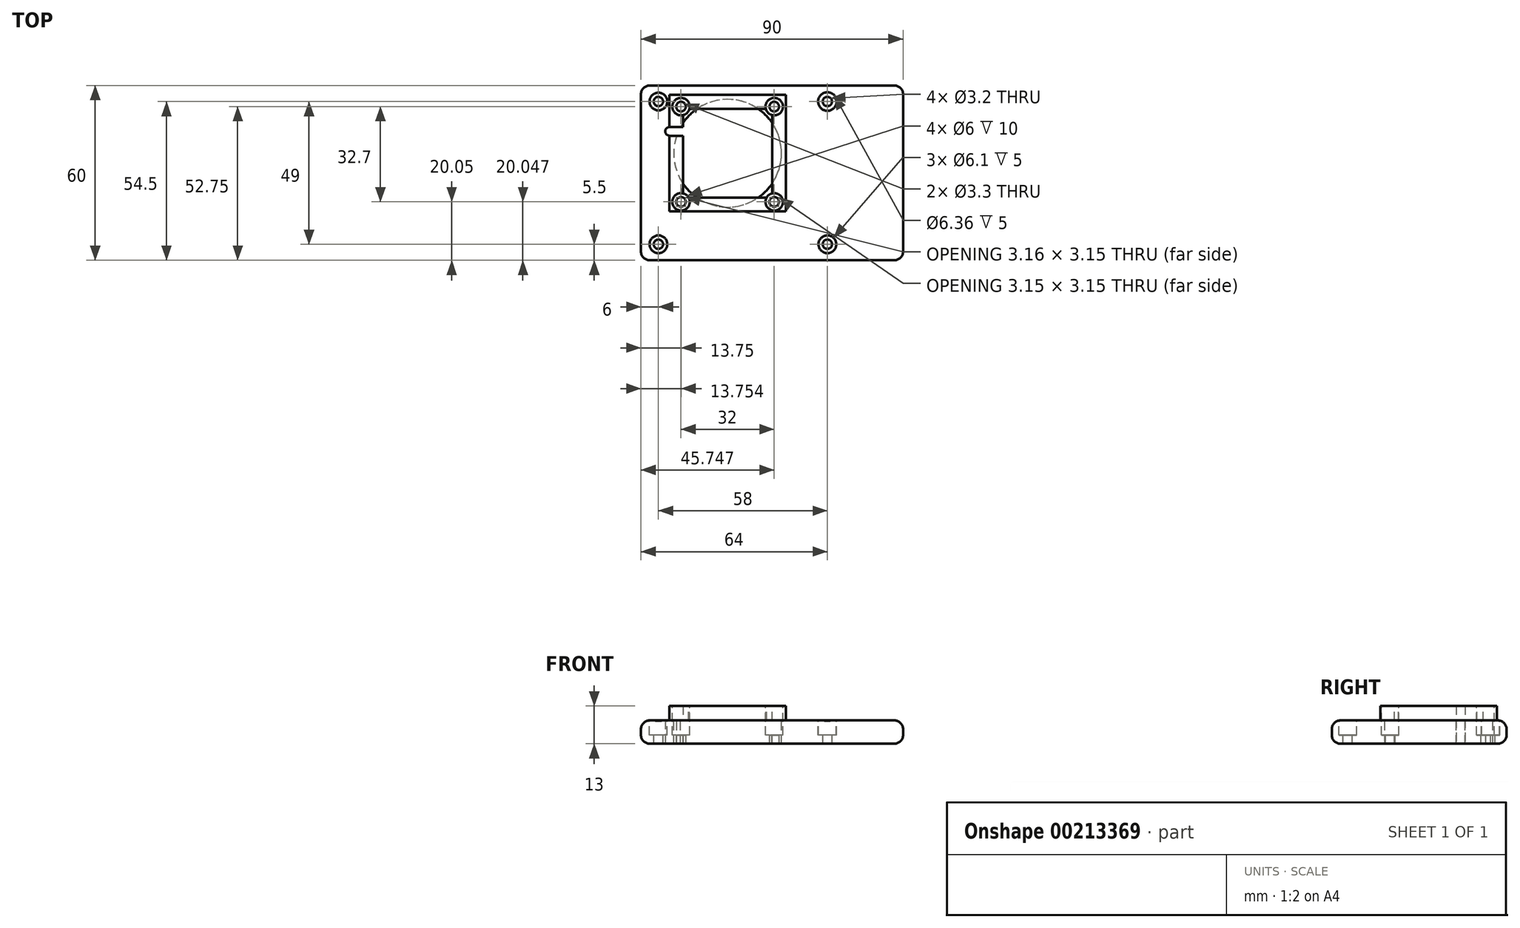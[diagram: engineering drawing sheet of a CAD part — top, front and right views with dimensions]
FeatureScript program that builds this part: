
annotation { "Feature Type Name" : "Feature", "Feature Type Description" : "" }
export const myFeature = defineFeature(function(context is Context, id is Id, definition is map)
    precondition{}
    {
        {
            var Q0;
            Q0=qCreatedBy(makeId("Top.planeOp"),FACE);
            var sketch = newSketch(context, id + "F0", { "sketchPlane" : qUnion([Q0])});
            skLineSegment(sketch, "E0.bottom", {"start": v(-45.78, -23.25) * mm, "end": v(38.22, -23.25) * mm});
            skLineSegment(sketch, "E0.top", {"start": v(-45.78, 36.75) * mm, "end": v(38.22, 36.75) * mm});
            skLineSegment(sketch, "E0.left", {"start": v(-48.78, -20.25) * mm, "end": v(-48.78, 33.75) * mm});
            skLineSegment(sketch, "E0.right", {"start": v(41.22, -20.25) * mm, "end": v(41.22, 33.75) * mm});
            skPoint(sketch, "E1.visualSharp", {"position": v(-48.78, 36.75) * mm});
            skArc(sketch, "E1.filletArc", {"start": v(-45.78, 36.75) * mm, "mid": v(-47.9, 35.87) * mm, "end": v(-48.78, 33.75) * mm});
            skPoint(sketch, "E2.visualSharp", {"position": v(41.22, 36.75) * mm});
            skArc(sketch, "E2.filletArc", {"start": v(41.22, 33.75) * mm, "mid": v(40.34, 35.87) * mm, "end": v(38.22, 36.75) * mm});
            skPoint(sketch, "E3.visualSharp", {"position": v(41.22, -23.25) * mm});
            skArc(sketch, "E3.filletArc", {"start": v(38.22, -23.25) * mm, "mid": v(40.34, -22.37) * mm, "end": v(41.22, -20.25) * mm});
            skPoint(sketch, "E4.visualSharp", {"position": v(-48.78, -23.25) * mm});
            skArc(sketch, "E4.filletArc", {"start": v(-48.78, -20.25) * mm, "mid": v(-47.9, -22.37) * mm, "end": v(-45.78, -23.25) * mm});
            skCircle(sketch, "E5", {"center": v(-42.78, -17.75) * mm, "radius": 1.6 * mm});
            skCircle(sketch, "E6", {"center": v(15.22, -17.75) * mm, "radius": 1.6 * mm});
            skCircle(sketch, "E7", {"center": v(-42.78, 31.25) * mm, "radius": 1.6 * mm});
            skCircle(sketch, "E8", {"center": v(15.22, 31.25) * mm, "radius": 1.6 * mm});
            skPoint(sketch, "E9", {"position": v(-29.78, 8.98) * mm});
            skPoint(sketch, "E10", {"position": v(2.22, -23.02) * mm});
            skLineSegment(sketch, "E11.bottom", {"start": v(-44.03, -20.25) * mm, "end": v(5.97, -20.25) * mm});
            skLineSegment(sketch, "E11.top", {"start": v(-44.03, 24.75) * mm, "end": v(5.97, 24.75) * mm});
            skLineSegment(sketch, "E11.left", {"start": v(-44.03, -20.25) * mm, "end": v(-44.03, 24.75) * mm});
            skLineSegment(sketch, "E11.right", {"start": v(5.97, -20.25) * mm, "end": v(5.97, 24.75) * mm});
            skLineSegment(sketch, "E12.bottom", {"start": v(-34.28, -15.25) * mm, "end": v(-3.78, -15.25) * mm});
            skLineSegment(sketch, "E12.top", {"start": v(-34.28, 15.25) * mm, "end": v(-3.78, 15.25) * mm});
            skLineSegment(sketch, "E12.left", {"start": v(-34.28, -15.25) * mm, "end": v(-34.28, 15.25) * mm});
            skLineSegment(sketch, "E12.right", {"start": v(-3.78, -15.25) * mm, "end": v(-3.78, 15.25) * mm});
            skCircle(sketch, "E13", {"center": v(-19.03, 0) * mm, "radius": 18.5 * mm});
            skLineSegment(sketch, "E14.bottom", {"start": v(0.97, 20) * mm, "end": v(-39.03, 20) * mm});
            skLineSegment(sketch, "E14.top", {"start": v(0.97, -20) * mm, "end": v(-39.03, -20) * mm});
            skLineSegment(sketch, "E14.left", {"start": v(0.97, 20) * mm, "end": v(0.97, -20) * mm});
            skLineSegment(sketch, "E14.right", {"start": v(-39.03, 20) * mm, "end": v(-39.03, -20) * mm});
            skCircle(sketch, "E15", {"center": v(-35.03, -16) * mm, "radius": 1.65 * mm});
            skCircle(sketch, "E16", {"center": v(-35.03, 16.7) * mm, "radius": 1.65 * mm});
            skCircle(sketch, "E17", {"center": v(-3.03, -16) * mm, "radius": 1.65 * mm});
            skCircle(sketch, "E18", {"center": v(-3.03, 16.7) * mm, "radius": 1.65 * mm});
            skCircle(sketch, "E19", {"center": v(15.22, 31.25) * mm, "radius": 3.05 * mm});
            skCircle(sketch, "E20", {"center": v(15.22, -17.75) * mm, "radius": 3.18 * mm});
            skCircle(sketch, "E21", {"center": v(-42.78, -17.75) * mm, "radius": 3.05 * mm});
            skCircle(sketch, "E22", {"center": v(-42.78, 31.25) * mm, "radius": 3.05 * mm});
            skLineSegment(sketch, "E23", {"start": v(-57.92, 59.7) * mm, "end": v(47.25, 59.7) * mm});
            skSolve(sketch);
        }
        {
            var Q0;
            {var subQ0=sQuery(id+"F0.wireOp",EDGE,"E13");var subQ1=sQuery(id+"F0.wireOp",EDGE,"E12.bottom");var subQ2=makeQuery(id+"F0.imprint","INTERSECT",VERTEX,{"disambiguationData":[OD(0.0)],"derivedFrom":[subQ1,subQ0]});Q0=makeQuery(id+"F0.imprint","IMPRINT",FACE,{"disambiguationData":[TD([[makeQuery(id+"F0.imprint","IMPRINT",EDGE,{"disambiguationData":[TD([[subQ2,-1.0]])],"derivedFrom":subQ1}),-1.0]])]});}
            var Q1;
            {var subQ0=sQuery(id+"F0.wireOp",EDGE,"E13");var subQ1=sQuery(id+"F0.wireOp",EDGE,"E12.right");var subQ2=makeQuery(id+"F0.imprint","INTERSECT",VERTEX,{"disambiguationData":[OD(0.0)],"derivedFrom":[subQ1,subQ0]});Q1=makeQuery(id+"F0.imprint","IMPRINT",FACE,{"disambiguationData":[TD([[makeQuery(id+"F0.imprint","IMPRINT",EDGE,{"disambiguationData":[TD([[subQ2,-1.0]])],"derivedFrom":subQ1}),-1.0]])]});}
            var Q2;
            {var subQ0=sQuery(id+"F0.wireOp",EDGE,"E13");var subQ1=sQuery(id+"F0.wireOp",EDGE,"E12.top");var subQ2=makeQuery(id+"F0.imprint","INTERSECT",VERTEX,{"disambiguationData":[OD(0.0)],"derivedFrom":[subQ1,subQ0]});Q2=makeQuery(id+"F0.imprint","IMPRINT",FACE,{"disambiguationData":[TD([[makeQuery(id+"F0.imprint","IMPRINT",EDGE,{"disambiguationData":[TD([[subQ2,-1.0]])],"derivedFrom":subQ1}),1.0]])]});}
            var Q3;
            {var subQ0=sQuery(id+"F0.wireOp",EDGE,"E13");var subQ1=sQuery(id+"F0.wireOp",EDGE,"E12.left");var subQ2=makeQuery(id+"F0.imprint","INTERSECT",VERTEX,{"disambiguationData":[OD(0.0)],"derivedFrom":[subQ1,subQ0]});Q3=makeQuery(id+"F0.imprint","IMPRINT",FACE,{"disambiguationData":[TD([[makeQuery(id+"F0.imprint","IMPRINT",EDGE,{"disambiguationData":[TD([[subQ2,-1.0]])],"derivedFrom":subQ1}),1.0]])]});}
            var Q4;
            Q4=makeQuery(id+"F0.imprint","IMPRINT",FACE,{"disambiguationData":[TD([[makeQuery(id+"F0.imprint","IMPRINT",EDGE,{"derivedFrom":sQuery(id+"F0.wireOp",EDGE,"E14.bottom")}),1.0]])]});
            extrude(context, id + "F1", {"entities" : qUnion([Q0, Q1, Q2, Q3, Q4]), "depth" : 5 * mm});
        }
        {
            var Q0;
            Q0=makeQuery(id+"F0.imprint","IMPRINT",FACE,{"disambiguationData":[TD([[makeQuery(id+"F0.imprint","IMPRINT",EDGE,{"derivedFrom":sQuery(id+"F0.wireOp",EDGE,"E0.bottom")}),1.0]])]});
            var Q1;
            {var subQ6=sQuery(id+"F0.wireOp",EDGE,"E11.bottom");Q1=makeQuery(id+"F0.imprint","IMPRINT",FACE,{"disambiguationData":[TD([[makeQuery(id+"F0.imprint","IMPRINT",EDGE,{"derivedFrom":subQ6}),1.0]])]});}
            var Q2;
            {var subQ0=sQuery(id+"F0.wireOp",EDGE,"E12.right");var subQ1=sQuery(id+"F0.wireOp",EDGE,"E12.top");var subQ2=makeQuery(id+"F0.imprint","INTERSECT",VERTEX,{"derivedFrom":[subQ1,subQ0]});Q2=makeQuery(id+"F0.imprint","IMPRINT",FACE,{"disambiguationData":[TD([[makeQuery(id+"F0.imprint","IMPRINT",EDGE,{"disambiguationData":[TD([[subQ2,1.0]])],"derivedFrom":subQ1}),-1.0]])]});}
            var Q3;
            {var subQ0=sQuery(id+"F0.wireOp",EDGE,"E12.left");var subQ1=sQuery(id+"F0.wireOp",EDGE,"E12.top");var subQ2=makeQuery(id+"F0.imprint","INTERSECT",VERTEX,{"derivedFrom":[subQ1,subQ0]});Q3=makeQuery(id+"F0.imprint","IMPRINT",FACE,{"disambiguationData":[TD([[makeQuery(id+"F0.imprint","IMPRINT",EDGE,{"disambiguationData":[TD([[subQ2,-1.0]])],"derivedFrom":subQ1}),-1.0]])]});}
            var Q4;
            {var subQ0=sQuery(id+"F0.wireOp",EDGE,"E13");var subQ1=sQuery(id+"F0.wireOp",EDGE,"E12.bottom");var subQ2=makeQuery(id+"F0.imprint","INTERSECT",VERTEX,{"disambiguationData":[OD(1.0)],"derivedFrom":[subQ1,subQ0]});Q4=makeQuery(id+"F0.imprint","IMPRINT",FACE,{"disambiguationData":[TD([[makeQuery(id+"F0.imprint","IMPRINT",EDGE,{"disambiguationData":[TD([[subQ2,-1.0]])],"derivedFrom":subQ1}),1.0]])]});}
            var Q5;
            {var subQ0=sQuery(id+"F0.wireOp",EDGE,"E13");var subQ1=sQuery(id+"F0.wireOp",EDGE,"E12.top");var subQ2=makeQuery(id+"F0.imprint","INTERSECT",VERTEX,{"disambiguationData":[OD(1.0)],"derivedFrom":[subQ1,subQ0]});Q5=makeQuery(id+"F0.imprint","IMPRINT",FACE,{"disambiguationData":[TD([[makeQuery(id+"F0.imprint","IMPRINT",EDGE,{"disambiguationData":[TD([[subQ2,-1.0]])],"derivedFrom":subQ1}),-1.0]])]});}
            var Q6;
            {var subQ0=sQuery(id+"F0.wireOp",EDGE,"E16");var subQ1=sQuery(id+"F0.wireOp",EDGE,"E12.top");var subQ2=makeQuery(id+"F0.imprint","INTERSECT",VERTEX,{"derivedFrom":[subQ1,subQ0]});Q6=makeQuery(id+"F0.imprint","IMPRINT",FACE,{"disambiguationData":[TD([[makeQuery(id+"F0.imprint","IMPRINT",EDGE,{"disambiguationData":[TD([[subQ2,-1.0]])],"derivedFrom":subQ1}),-1.0]])]});}
            var Q7;
            {var subQ0=sQuery(id+"F0.wireOp",EDGE,"E15");var subQ1=sQuery(id+"F0.wireOp",EDGE,"E12.bottom");var subQ2=makeQuery(id+"F0.imprint","INTERSECT",VERTEX,{"derivedFrom":[subQ1,subQ0]});Q7=makeQuery(id+"F0.imprint","IMPRINT",FACE,{"disambiguationData":[TD([[makeQuery(id+"F0.imprint","IMPRINT",EDGE,{"disambiguationData":[TD([[subQ2,-1.0]])],"derivedFrom":subQ1}),1.0]])]});}
            var Q8;
            Q8=makeQuery(id+"F0.imprint","IMPRINT",FACE,{"disambiguationData":[TD([[makeQuery(id+"F0.imprint","IMPRINT",EDGE,{"derivedFrom":sQuery(id+"F0.wireOp",EDGE,"E14.bottom")}),1.0]])]});
            var Q9;
            Q9=makeQuery(id+"F0.imprint","IMPRINT",FACE,{"disambiguationData":[TD([[makeQuery(id+"F0.imprint","IMPRINT",EDGE,{"derivedFrom":sQuery(id+"F0.wireOp",EDGE,"E5")}),-1.0]])]});
            var Q10;
            Q10=makeQuery(id+"F0.imprint","IMPRINT",FACE,{"disambiguationData":[TD([[makeQuery(id+"F0.imprint","IMPRINT",EDGE,{"derivedFrom":sQuery(id+"F0.wireOp",EDGE,"E6")}),-1.0]])]});
            var Q11;
            Q11=makeQuery(id+"F0.imprint","IMPRINT",FACE,{"disambiguationData":[TD([[makeQuery(id+"F0.imprint","IMPRINT",EDGE,{"derivedFrom":sQuery(id+"F0.wireOp",EDGE,"E8")}),-1.0]])]});
            var Q12;
            {var subQ2=sQuery(id+"F0.wireOp",EDGE,"E11.top");Q12=makeQuery(id+"F0.imprint","IMPRINT",FACE,{"disambiguationData":[TD([[makeQuery(id+"F0.imprint","IMPRINT",EDGE,{"derivedFrom":subQ2}),-1.0]])]});}
            var Q13;
            Q13=makeQuery(id+"F0.imprint","IMPRINT",FACE,{"disambiguationData":[TD([[makeQuery(id+"F0.imprint","IMPRINT",EDGE,{"derivedFrom":sQuery(id+"F0.wireOp",EDGE,"E7")}),-1.0]])]});
            extrude(context, id + "F2", {"entities" : qUnion([Q0, Q1, Q2, Q3, Q4, Q5, Q6, Q7, Q8, Q9, Q10, Q11, Q12, Q13]), "operationType" : NewBodyOperationType.ADD, "oppositeDirection" : true, "depth" : 8 * mm});
        }
        {
            var Q0;
            Q0=makeQuery(id+"F1.opExtrude","CAP_FACE",FACE,{"disambiguationData":[OSD([sQuery(id+"F0.wireOp",EDGE,"E7"),sQuery(id+"F0.wireOp",EDGE,"E11.bottom"),sQuery(id+"F0.wireOp",EDGE,"E11.top"),sQuery(id+"F0.wireOp",EDGE,"E11.left"),sQuery(id+"F0.wireOp",EDGE,"E11.right"),sQuery(id+"F0.wireOp",EDGE,"E12.bottom"),sQuery(id+"F0.wireOp",EDGE,"E12.top"),sQuery(id+"F0.wireOp",EDGE,"E12.left"),sQuery(id+"F0.wireOp",EDGE,"E12.right"),sQuery(id+"F0.wireOp",EDGE,"E15"),sQuery(id+"F0.wireOp",EDGE,"E16"),sQuery(id+"F0.wireOp",EDGE,"E17"),sQuery(id+"F0.wireOp",EDGE,"E18")])],"isStart":false});
            var sketch = newSketch(context, id + "F3", { "sketchPlane" : qUnion([Q0])});
            skCircle(sketch, "E24", {"center": v(-35.03, 16.7) * mm, "radius": 3 * mm});
            skCircle(sketch, "E25", {"center": v(-35.03, -16) * mm, "radius": 3 * mm});
            skCircle(sketch, "E26", {"center": v(-3.03, -16) * mm, "radius": 3 * mm});
            skCircle(sketch, "E27", {"center": v(-3.03, 16.7) * mm, "radius": 3 * mm});
            skSolve(sketch);
        }
        {
            var Q0;
            {var subQ2=sQuery(id+"F0.wireOp",EDGE,"E7");var subQ4=makeQuery(id+"F1.opExtrude","CAP_EDGE",EDGE,{"disambiguationData":[OSD([subQ2])],"isStart":false});Q0=makeQuery(id+"F3.imprint","IMPRINT",FACE,{"disambiguationData":[TD([[makeQuery(id+"F3.imprint","IMPRINT",EDGE,{"derivedFrom":subQ4}),-1.0]])]});}
            var Q1;
            {var subQ5=makeQuery(id+"F1.opExtrude","CAP_EDGE",EDGE,{"disambiguationData":[OSD([sQuery(id+"F0.wireOp",EDGE,"E16")])],"isStart":false});Q1=makeQuery(id+"F3.imprint","IMPRINT",FACE,{"disambiguationData":[TD([[makeQuery(id+"F3.imprint","IMPRINT",EDGE,{"derivedFrom":subQ5}),-1.0]])]});}
            var Q2;
            {var subQ5=makeQuery(id+"F1.opExtrude","CAP_EDGE",EDGE,{"disambiguationData":[OSD([sQuery(id+"F0.wireOp",EDGE,"E15")])],"isStart":false});Q2=makeQuery(id+"F3.imprint","IMPRINT",FACE,{"disambiguationData":[TD([[makeQuery(id+"F3.imprint","IMPRINT",EDGE,{"derivedFrom":subQ5}),-1.0]])]});}
            var Q3;
            {var subQ2=sQuery(id+"F0.wireOp",EDGE,"E7");var subQ7=makeQuery(id+"F1.opExtrude","CAP_EDGE",EDGE,{"disambiguationData":[OSD([subQ2])],"isStart":false});Q3=makeQuery(id+"F3.imprint","IMPRINT",FACE,{"disambiguationData":[TD([[makeQuery(id+"F3.imprint","IMPRINT",EDGE,{"derivedFrom":subQ7}),1.0]])]});}
            var Q4;
            {var subQ5=makeQuery(id+"F1.opExtrude","CAP_EDGE",EDGE,{"disambiguationData":[OSD([sQuery(id+"F0.wireOp",EDGE,"E16")])],"isStart":false});Q4=makeQuery(id+"F3.imprint","IMPRINT",FACE,{"disambiguationData":[TD([[makeQuery(id+"F3.imprint","IMPRINT",EDGE,{"derivedFrom":subQ5}),1.0]])]});}
            var Q5;
            {var subQ5=makeQuery(id+"F1.opExtrude","CAP_EDGE",EDGE,{"disambiguationData":[OSD([sQuery(id+"F0.wireOp",EDGE,"E15")])],"isStart":false});Q5=makeQuery(id+"F3.imprint","IMPRINT",FACE,{"disambiguationData":[TD([[makeQuery(id+"F3.imprint","IMPRINT",EDGE,{"derivedFrom":subQ5}),1.0]])]});}
            var Q6;
            {var subQ5=makeQuery(id+"F1.opExtrude","CAP_EDGE",EDGE,{"disambiguationData":[OSD([sQuery(id+"F0.wireOp",EDGE,"E17")])],"isStart":false});Q6=makeQuery(id+"F3.imprint","IMPRINT",FACE,{"disambiguationData":[TD([[makeQuery(id+"F3.imprint","IMPRINT",EDGE,{"derivedFrom":subQ5}),-1.0]])]});}
            var Q7;
            {var subQ5=makeQuery(id+"F1.opExtrude","CAP_EDGE",EDGE,{"disambiguationData":[OSD([sQuery(id+"F0.wireOp",EDGE,"E17")])],"isStart":false});Q7=makeQuery(id+"F3.imprint","IMPRINT",FACE,{"disambiguationData":[TD([[makeQuery(id+"F3.imprint","IMPRINT",EDGE,{"derivedFrom":subQ5}),1.0]])]});}
            var Q8;
            {var subQ5=makeQuery(id+"F1.opExtrude","CAP_EDGE",EDGE,{"disambiguationData":[OSD([sQuery(id+"F0.wireOp",EDGE,"E18")])],"isStart":false});Q8=makeQuery(id+"F3.imprint","IMPRINT",FACE,{"disambiguationData":[TD([[makeQuery(id+"F3.imprint","IMPRINT",EDGE,{"derivedFrom":subQ5}),-1.0]])]});}
            var Q9;
            {var subQ5=makeQuery(id+"F1.opExtrude","CAP_EDGE",EDGE,{"disambiguationData":[OSD([sQuery(id+"F0.wireOp",EDGE,"E18")])],"isStart":false});Q9=makeQuery(id+"F3.imprint","IMPRINT",FACE,{"disambiguationData":[TD([[makeQuery(id+"F3.imprint","IMPRINT",EDGE,{"derivedFrom":subQ5}),1.0]])]});}
            extrude(context, id + "F4", {"entities" : qUnion([Q0, Q1, Q2, Q3, Q4, Q5, Q6, Q7, Q8, Q9]), "operationType" : NewBodyOperationType.REMOVE, "oppositeDirection" : true, "depth" : 10 * mm});
        }
        {
            var Q0;
            Q0=makeQuery(id+"F0.imprint","IMPRINT",FACE,{"disambiguationData":[TD([[makeQuery(id+"F0.imprint","IMPRINT",EDGE,{"derivedFrom":sQuery(id+"F0.wireOp",EDGE,"E5")}),-1.0]])]});
            var Q1;
            Q1=makeQuery(id+"F0.imprint","IMPRINT",FACE,{"disambiguationData":[TD([[makeQuery(id+"F0.imprint","IMPRINT",EDGE,{"derivedFrom":sQuery(id+"F0.wireOp",EDGE,"E6")}),-1.0]])]});
            var Q2;
            Q2=makeQuery(id+"F0.imprint","IMPRINT",FACE,{"disambiguationData":[TD([[makeQuery(id+"F0.imprint","IMPRINT",EDGE,{"derivedFrom":sQuery(id+"F0.wireOp",EDGE,"E8")}),-1.0]])]});
            var Q3;
            Q3=makeQuery(id+"F0.imprint","IMPRINT",FACE,{"disambiguationData":[TD([[makeQuery(id+"F0.imprint","IMPRINT",EDGE,{"derivedFrom":sQuery(id+"F0.wireOp",EDGE,"E7")}),-1.0]])]});
            extrude(context, id + "F5", {"entities" : qUnion([Q0, Q1, Q2, Q3]), "operationType" : NewBodyOperationType.REMOVE, "oppositeDirection" : true, "depth" : 5 * mm});
        }
        {
            var Q0;
            Q0=makeQuery(id+"F2.opExtrude","CAP_FACE",FACE,{"disambiguationData":[OSD([sQuery(id+"F0.wireOp",EDGE,"E0.bottom"),sQuery(id+"F0.wireOp",EDGE,"E0.top"),sQuery(id+"F0.wireOp",EDGE,"E0.left"),sQuery(id+"F0.wireOp",EDGE,"E0.right"),sQuery(id+"F0.wireOp",EDGE,"E1.filletArc"),sQuery(id+"F0.wireOp",EDGE,"E2.filletArc"),sQuery(id+"F0.wireOp",EDGE,"E3.filletArc"),sQuery(id+"F0.wireOp",EDGE,"E4.filletArc"),sQuery(id+"F0.wireOp",EDGE,"E5"),sQuery(id+"F0.wireOp",EDGE,"E6"),sQuery(id+"F0.wireOp",EDGE,"E7"),sQuery(id+"F0.wireOp",EDGE,"E8"),sQuery(id+"F0.wireOp",EDGE,"E12.top"),sQuery(id+"F0.wireOp",EDGE,"E12.left"),sQuery(id+"F0.wireOp",EDGE,"E12.right"),sQuery(id+"F0.wireOp",EDGE,"E13"),sQuery(id+"F0.wireOp",EDGE,"E15"),sQuery(id+"F0.wireOp",EDGE,"E16"),sQuery(id+"F0.wireOp",EDGE,"E17"),sQuery(id+"F0.wireOp",EDGE,"E18")])],"isStart":false});
            var sketch = newSketch(context, id + "F6", { "sketchPlane" : qUnion([Q0])});
            skCircle(sketch, "E28", {"center": v(-38.96, 7.51) * mm, "radius": 1.5 * mm});
            skLineSegment(sketch, "E29", {"start": v(-38.96, 9.01) * mm, "end": v(-34.05, 9.01) * mm});
            skLineSegment(sketch, "E30", {"start": v(-38.96, 6.01) * mm, "end": v(-34.05, 6.01) * mm});
            skLineSegment(sketch, "E31", {"start": v(-34.05, 6.01) * mm, "end": v(-34.05, 9.01) * mm});
            skSolve(sketch);
        }
        {
            var Q0;
            {var subQ0=sQuery(id+"F6.wireOp",EDGE,"E28");var subQ1=makeQuery(id+"F6.imprint","INTERSECT",VERTEX,{"derivedFrom":[subQ0,sQuery(id+"F6.wireOp",EDGE,"E29")]});Q0=makeQuery(id+"F6.imprint","IMPRINT",FACE,{"disambiguationData":[TD([[makeQuery(id+"F6.imprint","IMPRINT",EDGE,{"disambiguationData":[TD([[subQ1,-1.0]])],"derivedFrom":subQ0}),1.0]])]});}
            var Q1;
            {var subQ0=sQuery(id+"F6.wireOp",EDGE,"E29");var subQ1=sQuery(id+"F6.wireOp",EDGE,"E28");var subQ2=makeQuery(id+"F6.imprint","INTERSECT",VERTEX,{"derivedFrom":[subQ1,subQ0]});Q1=makeQuery(id+"F6.imprint","IMPRINT",FACE,{"disambiguationData":[TD([[makeQuery(id+"F6.imprint","IMPRINT",EDGE,{"disambiguationData":[TD([[subQ2,1.0]])],"derivedFrom":subQ1}),-1.0]])]});}
            var Q2;
            {var subQ0=sQuery(id+"F6.wireOp",EDGE,"E31");Q2=makeQuery(id+"F6.imprint","IMPRINT",FACE,{"disambiguationData":[TD([[makeQuery(id+"F6.imprint","IMPRINT",EDGE,{"derivedFrom":subQ0}),1.0]])]});}
            extrude(context, id + "F7", {"entities" : qUnion([Q0, Q1, Q2]), "operationType" : NewBodyOperationType.REMOVE, "endBound" : BoundingType.THROUGH_ALL, "oppositeDirection" : true, "depth" : 25 * mm});
        }
        {
            var Q0;
            Q0=makeQuery(id+"F1.opExtrude","SWEPT_BODY",BODY,{"disambiguationData":[OSD([sQuery(id+"F0.wireOp",EDGE,"E12.bottom"),sQuery(id+"F0.wireOp",EDGE,"E12.top"),sQuery(id+"F0.wireOp",EDGE,"E12.left"),sQuery(id+"F0.wireOp",EDGE,"E12.right"),sQuery(id+"F0.wireOp",EDGE,"E14.bottom"),sQuery(id+"F0.wireOp",EDGE,"E14.top"),sQuery(id+"F0.wireOp",EDGE,"E14.left"),sQuery(id+"F0.wireOp",EDGE,"E14.right"),sQuery(id+"F0.wireOp",EDGE,"E15"),sQuery(id+"F0.wireOp",EDGE,"E16"),sQuery(id+"F0.wireOp",EDGE,"E17"),sQuery(id+"F0.wireOp",EDGE,"E18")])]});
            var Q1;
            Q1=qCreatedBy(makeId("Front.planeOp"),FACE);
            transform(context, id + "F8", {"entities" : qUnion([Q0]), "transformType" : TransformType.TRANSLATION_DISTANCE, "transformDirection" : qUnion([Q1]), "distance" : 100 * mm, "makeCopy" : false});
        }
        {
            var Q0;
            Q0=makeQuery(id+"F1.opExtrude","SWEPT_BODY",BODY,{"disambiguationData":[OSD([sQuery(id+"F0.wireOp",EDGE,"E12.bottom"),sQuery(id+"F0.wireOp",EDGE,"E12.top"),sQuery(id+"F0.wireOp",EDGE,"E12.left"),sQuery(id+"F0.wireOp",EDGE,"E12.right"),sQuery(id+"F0.wireOp",EDGE,"E14.bottom"),sQuery(id+"F0.wireOp",EDGE,"E14.top"),sQuery(id+"F0.wireOp",EDGE,"E14.left"),sQuery(id+"F0.wireOp",EDGE,"E14.right"),sQuery(id+"F0.wireOp",EDGE,"E15"),sQuery(id+"F0.wireOp",EDGE,"E16"),sQuery(id+"F0.wireOp",EDGE,"E17"),sQuery(id+"F0.wireOp",EDGE,"E18")])]});
            var Q1;
            Q1=qCreatedBy(makeId("Front.planeOp"),FACE);
            mirror(context, id + "F9", {"entities" : qUnion([Q0]), "mirrorPlane" : qUnion([Q1])});
        }
        {
            var Q0;
            Q0=makeQuery(id+"F1.opExtrude","SWEPT_BODY",BODY,{"disambiguationData":[OSD([sQuery(id+"F0.wireOp",EDGE,"E12.bottom"),sQuery(id+"F0.wireOp",EDGE,"E12.top"),sQuery(id+"F0.wireOp",EDGE,"E12.left"),sQuery(id+"F0.wireOp",EDGE,"E12.right"),sQuery(id+"F0.wireOp",EDGE,"E14.bottom"),sQuery(id+"F0.wireOp",EDGE,"E14.top"),sQuery(id+"F0.wireOp",EDGE,"E14.left"),sQuery(id+"F0.wireOp",EDGE,"E14.right"),sQuery(id+"F0.wireOp",EDGE,"E15"),sQuery(id+"F0.wireOp",EDGE,"E16"),sQuery(id+"F0.wireOp",EDGE,"E17"),sQuery(id+"F0.wireOp",EDGE,"E18")])]});
            deleteBodies(context, id + "F10", {"entities" : qUnion([Q0])});
        }
        {
            var Q0;
            Q0=makeQuery(id+"F9.opPattern","COPY",EDGE,{"derivedFrom":makeQuery(id+"F2.opExtrude","CAP_EDGE",EDGE,{"disambiguationData":[OSD([sQuery(id+"F0.wireOp",EDGE,"E0.top")])],"isStart":false}),"instanceName":"1"});
            var Q1;
            Q1=makeQuery(id+"F9.opPattern","COPY",EDGE,{"derivedFrom":makeQuery(id+"F2.opExtrude","CAP_EDGE",EDGE,{"disambiguationData":[OSD([sQuery(id+"F0.wireOp",EDGE,"E0.top")])],"isStart":true}),"instanceName":"1"});
            fillet(context, id + "F11", {"entities" : qUnion([Q0, Q1]), "radius" : 3 * mm, "tangentPropagation" : true, "allowEdgeOverflow" : false});
        }
    });
